# Revit family: Betonafstandsklods med wire 35-40-50
name_source: partatom
category: Generic Models
units: mm (PartAtom-declared; Revit-internal decimal feet)

## family parameters
Always vertical = No
Can host rebar = No
Cut with Voids When Loaded = No
Part Type = Normal
Room Calculation Point = No
Round Connector Dimension = Use Diameter
Shared = No
Work Plane-Based = Yes

## types (1)
- Betonafstandsklods med wire 35-40-50
    Bottom Curve = 28 mm  [stored 0.0918635 ft]
    Default Elevation = 1219 mm
    Height = 47 mm  [stored 0.154199 ft]
    Metal = Metal
    Numbers = Wall Texture, Orange Peel
    Side Curve = 28 mm  [stored 0.0918635 ft]
    Side Curve R = 35 mm  [stored 0.114829 ft]
    Technical Data Sheet = https://haucon.dk
    Thickness = 25 mm  [stored 0.082021 ft]
    Top Curve = 13 mm
    Top Curve R = 25 mm  [stored 0.082021 ft]
    Website Link = https://haucon.dk
    Width = 57 mm  [stored 0.187008 ft]
    concrete = Concrete, C50/60

note: [stored X ft] marks values corroborated as IEEE doubles in the binary element streams (Revit-internal decimal feet)

## geometry (parser evidence)
native form markers: Sweep x2
no freeform markers — native parametric forms only
